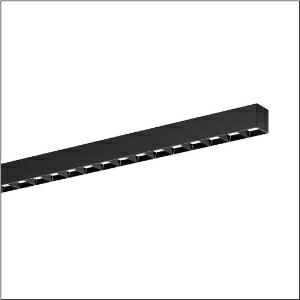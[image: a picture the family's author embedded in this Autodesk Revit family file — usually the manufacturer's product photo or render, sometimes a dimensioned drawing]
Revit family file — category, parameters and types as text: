
# Revit family: silica_r__21_51mx24tctab_feaf
name_source: partatom
category: Lighting Fixtures
units: mm (PartAtom-declared; Revit-internal decimal feet)

## family parameters
Cut with Voids When Loaded = No
Host = Face
Light Source = No
Part Type = Normal
Room Calculation Point = No
Round Connector Dimension = Use Diameter
Shared = No

## types (1)
- --- (1 x LED, 8200 lm, 81.1 W, 6500K)
    Apparent Load = 81 VA
    CIE Flux Codes = 74 94 99 100 100
    Color Rendering = 80
    Color Temperature = 6500K
    Default Elevation = 1800 mm
    Description = Silica® 21, office luminaire, primary light control with darklight reflector, of PMMA, black, light emission: direct distribution, primary light characteristic: asymmetric, installation type: surface-mounted, LED, rated luminous flux: 8.200lm, luminous efficacy: 96lm/W, light colour: 8tw, colour temperature: 2700..6500K, control gear: ECG DALI, with terminal, 3+2-pole, max. 2.5mm², mains connection: 220..240V, AC, 50/60Hz, rated input power: 85.2W, luminaire housing, of aluminium, jet black (RAL 9005), length: 3.004mm, width: 53mm, height: 53mm, protection rating (complete): IP20, insulation class (complete): insulation class I (protective earthing), certification: CE, permissible operating ambient temperature: 0..+35°C, standard: EN 50419, packaging unit: 1 piece
    Height = 0 mm  [stored 0 ft]
    Lamp = 1 x LED
    Lamp Light Flux = 8200 lm
    Lamp Power = 81.1 W
    Lamp count = 1
    Length = 3004 mm
    Luminous efficacy = 101 lm/W
    Manufacturer = Siteco
    ModVariant = No
    Model = 51MX24TCTAB
    Mounting Place = Ceiling
    Mounting Type = Recessed
    Number of Poles = 1
    OnlyDefault = Yes
    Power Factor = 1
    Product Name = Silica® 21
    Product group = office luminaire | ceiling recessed
    ProductGroupID = 401
    Protection Class = Protection class I
    Protection Degree = IP 20
    RLX_Detail_Level = 1
    RLX_Emergency_Light_Flux = 0 lm
    RLX_Emergency_Type = 0
    RLX_Emergency_Type_DB = No
    RlxData = <blob elided: 61737 chars, md5=cdce75a3>
    Socket = socket
    Standby Power = 0 W
    System Light Flux = 8200 lm
    System Power = 81 W
    Type Comments = individual setting
    Type Image = l_1297756.jpg
    URL = http://relux.com
    VarID = @adj_071311
    Voltage = 0 V
    Weight = 0.00 kg
    Width = 53 mm

note: [stored X ft] marks values corroborated as IEEE doubles in the binary element streams (Revit-internal decimal feet)

## geometry (parser evidence)
native form markers: Blend x4, Sweep x10
no freeform markers — native parametric forms only
